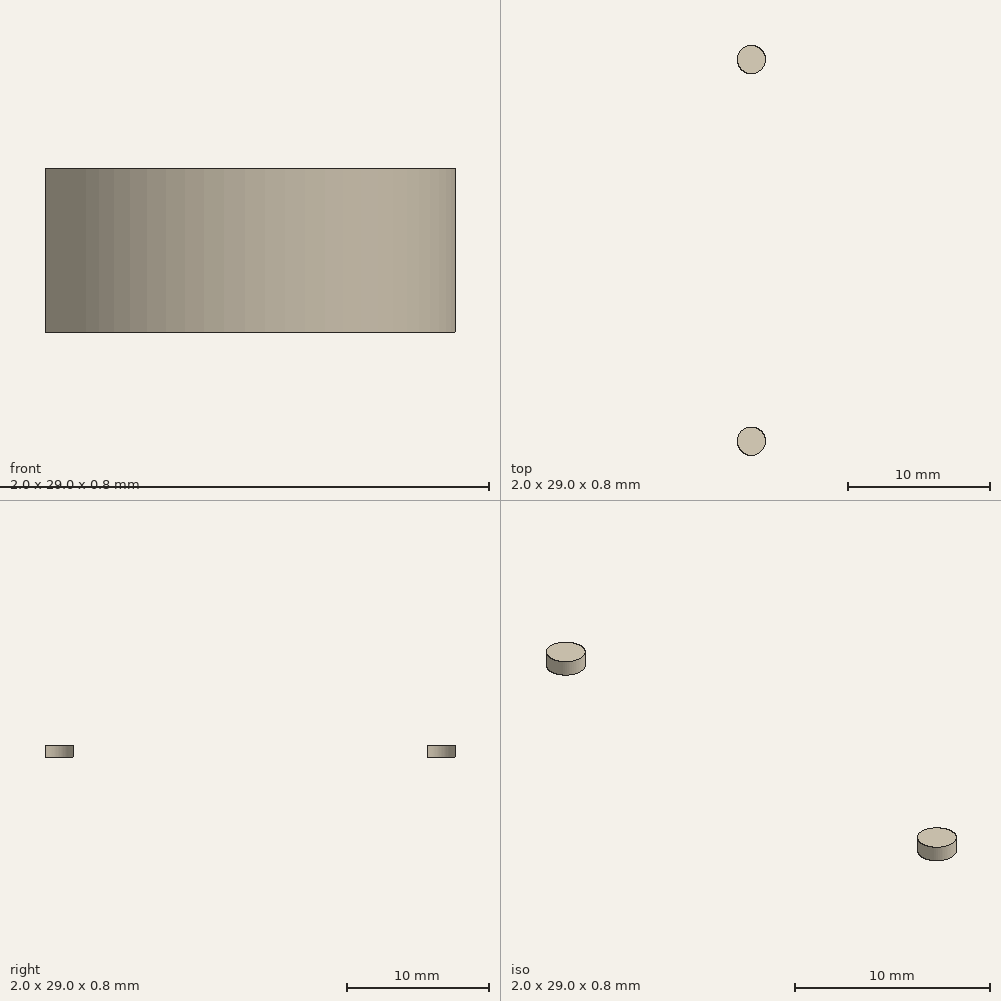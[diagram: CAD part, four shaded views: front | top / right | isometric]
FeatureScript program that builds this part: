
annotation { "Feature Type Name" : "Feature", "Feature Type Description" : "" }
export const myFeature = defineFeature(function(context is Context, id is Id, definition is map)
    precondition{}
    {
        {
            var Q0;
            Q0=qCreatedBy(makeId("Top.planeOp"),FACE);
            var sketch = newSketch(context, id + "F0", { "sketchPlane" : qUnion([Q0])});
            skLineSegment(sketch, "E0.bottom", {"start": v(0, 0) * mm, "end": v(48.4, 0) * mm});
            skLineSegment(sketch, "E0.top", {"start": v(0, 95) * mm, "end": v(48.4, 95) * mm});
            skLineSegment(sketch, "E0.left", {"start": v(0, 0) * mm, "end": v(0, 95) * mm});
            skLineSegment(sketch, "E0.right", {"start": v(48.4, 0) * mm, "end": v(48.4, 95) * mm});
            skSolve(sketch);
        }
        {
            var Q0;
            Q0=makeQuery(id+"F0.imprint","IMPRINT",FACE,{"disambiguationData":[TD([[makeQuery(id+"F0.imprint","IMPRINT",EDGE,{"derivedFrom":sQuery(id+"F0.wireOp",EDGE,"E0.bottom")}),1.0]])]});
            extrude(context, id + "F1", {"entities" : qUnion([Q0]), "depth" : 0.8 * mm});
        }
        {
            var Q0;
            Q0=makeQuery(id+"F1.opExtrude","CAP_FACE",FACE,{"disambiguationData":[OSD([sQuery(id+"F0.wireOp",EDGE,"E0.bottom"),sQuery(id+"F0.wireOp",EDGE,"E0.top"),sQuery(id+"F0.wireOp",EDGE,"E0.left"),sQuery(id+"F0.wireOp",EDGE,"E0.right")])],"isStart":false});
            var sketch = newSketch(context, id + "F2", { "sketchPlane" : qUnion([Q0])});
            skLineSegment(sketch, "E1", {"start": v(5, 95) * mm, "end": v(0, 90) * mm});
            skLineSegment(sketch, "E2", {"start": v(24.2, 95) * mm, "end": v(24.2, 0) * mm, "construction": true});
            skLineSegment(sketch, "E3.0.MirrorCS", {"start": v(43.4, 95) * mm, "end": v(48.4, 90) * mm});
            skSolve(sketch);
        }
        {
            var Q0;
            {var subQ1=sQuery(id+"F2.wireOp",EDGE,"E1");Q0=makeQuery(id+"F2.imprint","IMPRINT",FACE,{"disambiguationData":[TD([[makeQuery(id+"F2.imprint","IMPRINT",EDGE,{"derivedFrom":subQ1}),-1.0]])]});}
            var Q1;
            {var subQ1=sQuery(id+"F2.wireOp",EDGE,"E3.0.MirrorCS");Q1=makeQuery(id+"F2.imprint","IMPRINT",FACE,{"disambiguationData":[TD([[makeQuery(id+"F2.imprint","IMPRINT",EDGE,{"derivedFrom":subQ1}),1.0]])]});}
            extrude(context, id + "F3", {"entities" : qUnion([Q0, Q1]), "operationType" : NewBodyOperationType.REMOVE, "oppositeDirection" : true, "depth" : 25 * mm});
        }
        {
            var Q0;
            Q0=makeQuery(id+"F1.opExtrude","CAP_FACE",FACE,{"disambiguationData":[OSD([sQuery(id+"F0.wireOp",EDGE,"E0.bottom"),sQuery(id+"F0.wireOp",EDGE,"E0.top"),sQuery(id+"F0.wireOp",EDGE,"E0.left"),sQuery(id+"F0.wireOp",EDGE,"E0.right")])],"isStart":false});
            var sketch = newSketch(context, id + "F4", { "sketchPlane" : qUnion([Q0])});
            skLineSegment(sketch, "E4", {"start": v(0, 45) * mm, "end": v(-6.62, 38.38) * mm});
            skLineSegment(sketch, "E5", {"start": v(24.2, 95) * mm, "end": v(24.2, 0) * mm, "construction": true});
            skLineSegment(sketch, "E6", {"start": v(-6.62, 38.38) * mm, "end": v(-14.18, 38.38) * mm});
            skArc(sketch, "E7", {"start": v(-14.18, 38.38) * mm, "mid": v(-2.94, 11.24) * mm, "end": v(24.2, 0) * mm});
            skLineSegment(sketch, "E8.0.MirrorCS", {"start": v(48.4, 45) * mm, "end": v(55.02, 38.38) * mm});
            skLineSegment(sketch, "E9.0.MirrorCS", {"start": v(55.02, 38.38) * mm, "end": v(62.58, 38.38) * mm});
            skArc(sketch, "E10.0.MirrorCS", {"start": v(62.58, 38.38) * mm, "mid": v(51.34, 11.24) * mm, "end": v(24.2, 0) * mm});
            skSolve(sketch);
        }
        {
            var Q0;
            {var subQ3=sQuery(id+"F4.wireOp",EDGE,"E4");Q0=makeQuery(id+"F4.imprint","IMPRINT",FACE,{"disambiguationData":[TD([[makeQuery(id+"F4.imprint","IMPRINT",EDGE,{"derivedFrom":subQ3}),1.0]])]});}
            var Q1;
            {var subQ9=makeQuery(id+"F3.boolean.opBoolean","COPY",EDGE,{"derivedFrom":makeQuery(id+"F3.opExtrude","CAP_EDGE",EDGE,{"disambiguationData":[OSD([sQuery(id+"F2.wireOp",EDGE,"E1")])],"isStart":true})});Q1=makeQuery(id+"F4.imprint","IMPRINT",FACE,{"disambiguationData":[TD([[makeQuery(id+"F4.imprint","IMPRINT",EDGE,{"derivedFrom":subQ9}),1.0]])]});}
            var Q2;
            {var subQ4=sQuery(id+"F4.wireOp",EDGE,"E8.0.MirrorCS");Q2=makeQuery(id+"F4.imprint","IMPRINT",FACE,{"disambiguationData":[TD([[makeQuery(id+"F4.imprint","IMPRINT",EDGE,{"derivedFrom":subQ4}),-1.0]])]});}
            extrude(context, id + "F5", {"entities" : qUnion([Q0, Q1, Q2]), "operationType" : NewBodyOperationType.ADD, "oppositeDirection" : true, "depth" : 0.8 * mm});
        }
        {
            var Q0;
            {var subQ0=makeQuery(id+"F1.opExtrude","CAP_EDGE",EDGE,{"disambiguationData":[OSD([sQuery(id+"F0.wireOp",EDGE,"E0.left")])],"isStart":false});var subQ3=makeQuery(id+"F1.opExtrude","CAP_EDGE",EDGE,{"disambiguationData":[OSD([sQuery(id+"F0.wireOp",EDGE,"E0.bottom")])],"isStart":false});var subQ4=makeQuery(id+"F4.imprint","INTERSECT",VERTEX,{"derivedFrom":[subQ3,subQ0]});Q0=makeQuery(id+"F4.imprint","IMPRINT",FACE,{"disambiguationData":[TD([[makeQuery(id+"F4.imprint","IMPRINT",EDGE,{"disambiguationData":[TD([[subQ4,-1.0]])],"derivedFrom":subQ0}),-1.0]])]});}
            var Q1;
            {var subQ0=makeQuery(id+"F1.opExtrude","CAP_EDGE",EDGE,{"disambiguationData":[OSD([sQuery(id+"F0.wireOp",EDGE,"E0.right")])],"isStart":false});var subQ3=makeQuery(id+"F1.opExtrude","CAP_EDGE",EDGE,{"disambiguationData":[OSD([sQuery(id+"F0.wireOp",EDGE,"E0.bottom")])],"isStart":false});var subQ4=makeQuery(id+"F4.imprint","INTERSECT",VERTEX,{"derivedFrom":[subQ3,subQ0]});Q1=makeQuery(id+"F4.imprint","IMPRINT",FACE,{"disambiguationData":[TD([[makeQuery(id+"F4.imprint","IMPRINT",EDGE,{"disambiguationData":[TD([[subQ4,-1.0]])],"derivedFrom":subQ0}),1.0]])]});}
            extrude(context, id + "F6", {"entities" : qUnion([Q0, Q1]), "operationType" : NewBodyOperationType.REMOVE, "oppositeDirection" : true, "depth" : 25 * mm});
        }
        {
            var Q0;
            {var subQ0=sQuery(id+"F0.wireOp",EDGE,"E0.top");var subQ1=sQuery(id+"F0.wireOp",EDGE,"E0.left");var subQ2=sQuery(id+"F0.wireOp",EDGE,"E0.right");Q0=makeQuery(id+"F5.boolean.opBoolean","MERGE",FACE,{"derivedFrom":[makeQuery(id+"F1.opExtrude","CAP_FACE",FACE,{"disambiguationData":[OSD([sQuery(id+"F0.wireOp",EDGE,"E0.bottom"),subQ0,subQ1,subQ2])],"isStart":false}),makeQuery(id+"F5.opExtrude","CAP_FACE",FACE,{"disambiguationData":[OSD([subQ0,subQ1,subQ2,sQuery(id+"F2.wireOp",EDGE,"E1"),sQuery(id+"F2.wireOp",EDGE,"E3.0.MirrorCS"),sQuery(id+"F4.wireOp",EDGE,"E4"),sQuery(id+"F4.wireOp",EDGE,"E6"),sQuery(id+"F4.wireOp",EDGE,"E7"),sQuery(id+"F4.wireOp",EDGE,"E8.0.MirrorCS"),sQuery(id+"F4.wireOp",EDGE,"E9.0.MirrorCS"),sQuery(id+"F4.wireOp",EDGE,"E10.0.MirrorCS")])],"isStart":true})]});}
            var sketch = newSketch(context, id + "F7", { "sketchPlane" : qUnion([Q0])});
            skCircle(sketch, "E11", {"center": v(2, 80) * mm, "radius": 1 * mm});
            skLineSegment(sketch, "E12", {"start": v(24.2, 95) * mm, "end": v(24.2, 0) * mm, "construction": true});
            skCircle(sketch, "E13", {"center": v(2, 53) * mm, "radius": 1 * mm});
            skCircle(sketch, "E14.0.MirrorC", {"center": v(46.4, 80) * mm, "radius": 1 * mm});
            skCircle(sketch, "E15.0.MirrorC", {"center": v(46.4, 53) * mm, "radius": 1 * mm});
            skSolve(sketch);
        }
        {
            var Q0;
            Q0=makeQuery(id+"F7.imprint","IMPRINT",FACE,{"disambiguationData":[TD([[makeQuery(id+"F7.imprint","IMPRINT",EDGE,{"derivedFrom":sQuery(id+"F7.wireOp",EDGE,"E11")}),1.0]])]});
            var Q1;
            Q1=makeQuery(id+"F7.imprint","IMPRINT",FACE,{"disambiguationData":[TD([[makeQuery(id+"F7.imprint","IMPRINT",EDGE,{"derivedFrom":sQuery(id+"F7.wireOp",EDGE,"E13")}),1.0]])]});
            var Q2;
            Q2=makeQuery(id+"F7.imprint","IMPRINT",FACE,{"disambiguationData":[TD([[makeQuery(id+"F7.imprint","IMPRINT",EDGE,{"derivedFrom":sQuery(id+"F7.wireOp",EDGE,"E15.0.MirrorC")}),-1.0]])]});
            var Q3;
            Q3=makeQuery(id+"F7.imprint","IMPRINT",FACE,{"disambiguationData":[TD([[makeQuery(id+"F7.imprint","IMPRINT",EDGE,{"derivedFrom":sQuery(id+"F7.wireOp",EDGE,"E14.0.MirrorC")}),-1.0]])]});
            extrude(context, id + "F8", {"entities" : qUnion([Q0, Q1, Q2, Q3]), "operationType" : NewBodyOperationType.REMOVE, "oppositeDirection" : true, "depth" : 25 * mm});
        }
        {
            var Q0;
            {var subQ0=sQuery(id+"F0.wireOp",EDGE,"E0.top");var subQ1=sQuery(id+"F0.wireOp",EDGE,"E0.left");var subQ2=sQuery(id+"F0.wireOp",EDGE,"E0.right");Q0=makeQuery(id+"F5.boolean.opBoolean","MERGE",FACE,{"derivedFrom":[makeQuery(id+"F1.opExtrude","CAP_FACE",FACE,{"disambiguationData":[OSD([sQuery(id+"F0.wireOp",EDGE,"E0.bottom"),subQ0,subQ1,subQ2])],"isStart":false}),makeQuery(id+"F5.opExtrude","CAP_FACE",FACE,{"disambiguationData":[OSD([subQ0,subQ1,subQ2,sQuery(id+"F2.wireOp",EDGE,"E1"),sQuery(id+"F2.wireOp",EDGE,"E3.0.MirrorCS"),sQuery(id+"F4.wireOp",EDGE,"E4"),sQuery(id+"F4.wireOp",EDGE,"E6"),sQuery(id+"F4.wireOp",EDGE,"E7"),sQuery(id+"F4.wireOp",EDGE,"E8.0.MirrorCS"),sQuery(id+"F4.wireOp",EDGE,"E9.0.MirrorCS"),sQuery(id+"F4.wireOp",EDGE,"E10.0.MirrorCS")])],"isStart":true})]});}
            var sketch = newSketch(context, id + "F9", { "sketchPlane" : qUnion([Q0])});
            skLineSegment(sketch, "E16", {"start": v(59.15, 66.5) * mm, "end": v(-14.9, 66.5) * mm, "construction": true});
            skLineSegment(sketch, "E17", {"start": v(24.2, 95) * mm, "end": v(24.2, 0) * mm, "construction": true});
            skLineSegment(sketch, "E18.bottom", {"start": v(3.8, 70.65) * mm, "end": v(21.2, 70.65) * mm});
            skLineSegment(sketch, "E18.top", {"start": v(3.8, 62.35) * mm, "end": v(21.2, 62.35) * mm});
            skLineSegment(sketch, "E18.left", {"start": v(3.8, 70.65) * mm, "end": v(3.8, 62.35) * mm});
            skLineSegment(sketch, "E18.right", {"start": v(21.2, 70.65) * mm, "end": v(21.2, 62.35) * mm});
            skPoint(sketch, "E19", {"position": v(3.8, 66.5) * mm});
            skLineSegment(sketch, "E20.0.MirrorCS", {"start": v(44.6, 70.65) * mm, "end": v(27.2, 70.65) * mm});
            skLineSegment(sketch, "E21.0.MirrorCS", {"start": v(27.2, 70.65) * mm, "end": v(27.2, 62.35) * mm});
            skLineSegment(sketch, "E22.0.MirrorCS", {"start": v(44.6, 62.35) * mm, "end": v(27.2, 62.35) * mm});
            skLineSegment(sketch, "E23.0.MirrorCS", {"start": v(44.6, 70.65) * mm, "end": v(44.6, 62.35) * mm});
            skLineSegment(sketch, "E24", {"start": v(2, 80) * mm, "end": v(2, 53) * mm, "construction": true});
            skPoint(sketch, "E25", {"position": v(2, 66.5) * mm});
            skSolve(sketch);
        }
        {
            var Q0;
            Q0=makeQuery(id+"F9.imprint","IMPRINT",FACE,{"disambiguationData":[TD([[makeQuery(id+"F9.imprint","IMPRINT",EDGE,{"derivedFrom":sQuery(id+"F9.wireOp",EDGE,"E18.bottom")}),-1.0]])]});
            var Q1;
            Q1=makeQuery(id+"F9.imprint","IMPRINT",FACE,{"disambiguationData":[TD([[makeQuery(id+"F9.imprint","IMPRINT",EDGE,{"derivedFrom":sQuery(id+"F9.wireOp",EDGE,"E20.0.MirrorCS")}),1.0]])]});
            extrude(context, id + "F10", {"entities" : qUnion([Q0, Q1]), "operationType" : NewBodyOperationType.REMOVE, "oppositeDirection" : true, "depth" : 25 * mm});
        }
    });
